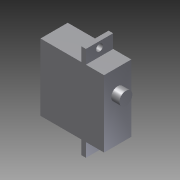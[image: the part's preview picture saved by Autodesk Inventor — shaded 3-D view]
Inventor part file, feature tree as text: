
AUTODESK INVENTOR PART (.ipt)
format: ipt  version: 2012 (Build 160160000, 160)  size: 105,984 bytes
history: native  units: mm
features: extrude x4, sketch x2
ambient origin geometry x8: Origin, YZ Plane, XZ Plane, XY Plane, X Axis, Y Axis, Z Axis, Center Point
bodies: Solid1 (feature_tree)
feature tree (6):
  sketch  "Sketch1"  dims[d0=12.0mm d1=29.5mm]
  extrude  "Extrusion1"  Depth=29.5mm
  extrude  "Extrusion2"  Depth=6.0mm
  extrude  "Extrusion3"  Depth=3.0mm
  extrude  "Extrusion5"  Depth=3.0mm
  sketch  "Sketch3"  dims[d2=6.0mm d3=6.0mm d4=3.0mm d5=3.0mm d6=20.0mm d7=0.0mm d8=2.0mm d9=0.0mm d10=8.0mm d11=0.0mm d18=5.7mm d19=10.0mm d20=3.6mm d21=0.0mm d23=2.5mm d24=2.5mm d25=3.5mm d26=6.0mm d27=6.0mm d28=6.0mm]
